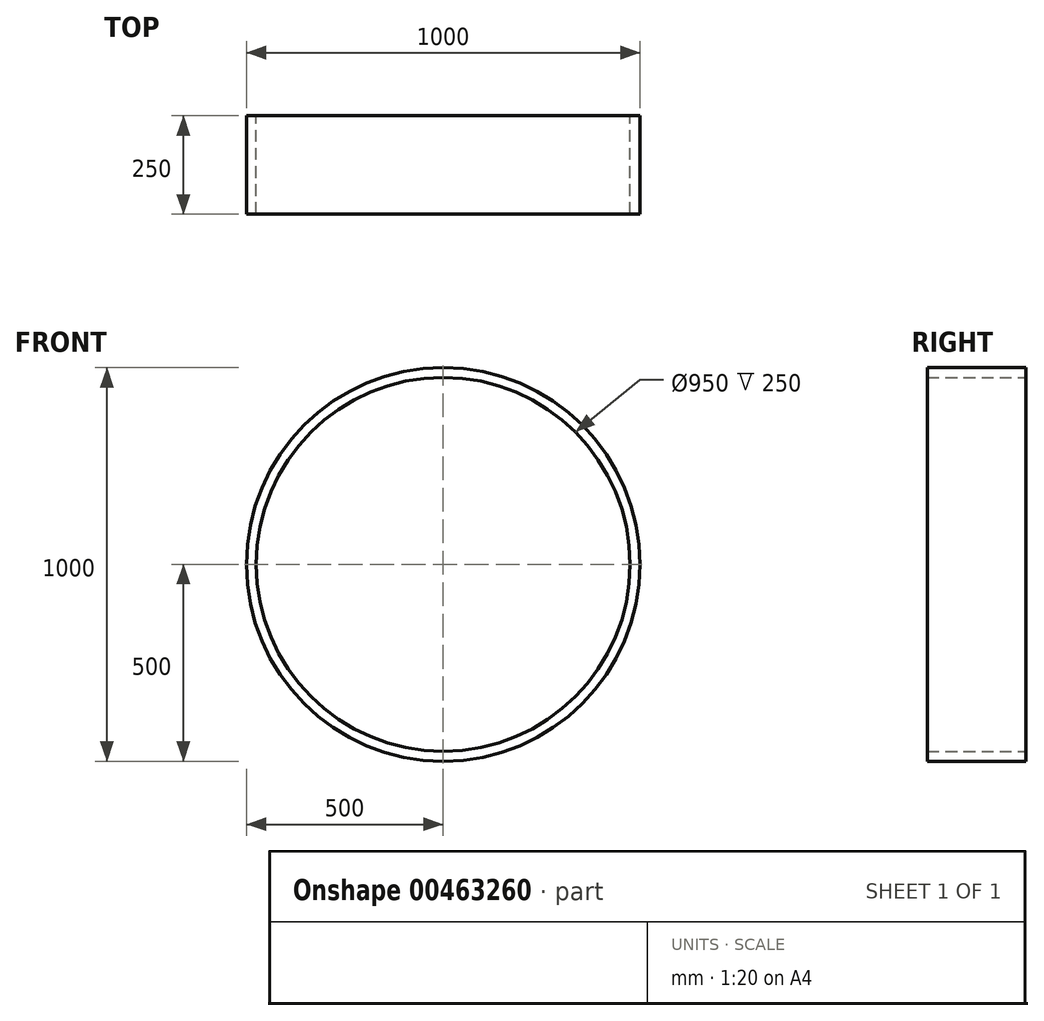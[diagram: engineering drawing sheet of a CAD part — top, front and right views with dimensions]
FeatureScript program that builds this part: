
annotation { "Feature Type Name" : "Feature", "Feature Type Description" : "" }
export const myFeature = defineFeature(function(context is Context, id is Id, definition is map)
    precondition{}
    {
        {
            var Q0;
            Q0=qCreatedBy(makeId("Front.planeOp"),FACE);
            var sketch = newSketch(context, id + "F0", { "sketchPlane" : qUnion([Q0])});
            skCircle(sketch, "E0", {"center": v(0, 0) * mm, "radius": 500 * mm});
            skCircle(sketch, "E1", {"center": v(0, 0) * mm, "radius": 475 * mm});
            skPoint(sketch, "E2", {"position": v(0, -486.83) * mm});
            skSolve(sketch);
        }
        {
            var Q0;
            Q0 = qSketchRegion(id + "F0", true);
            extrude(context, id + "F1", {"entities" : qUnion([Q0]), "depth" : 250 * mm});
        }
    });
